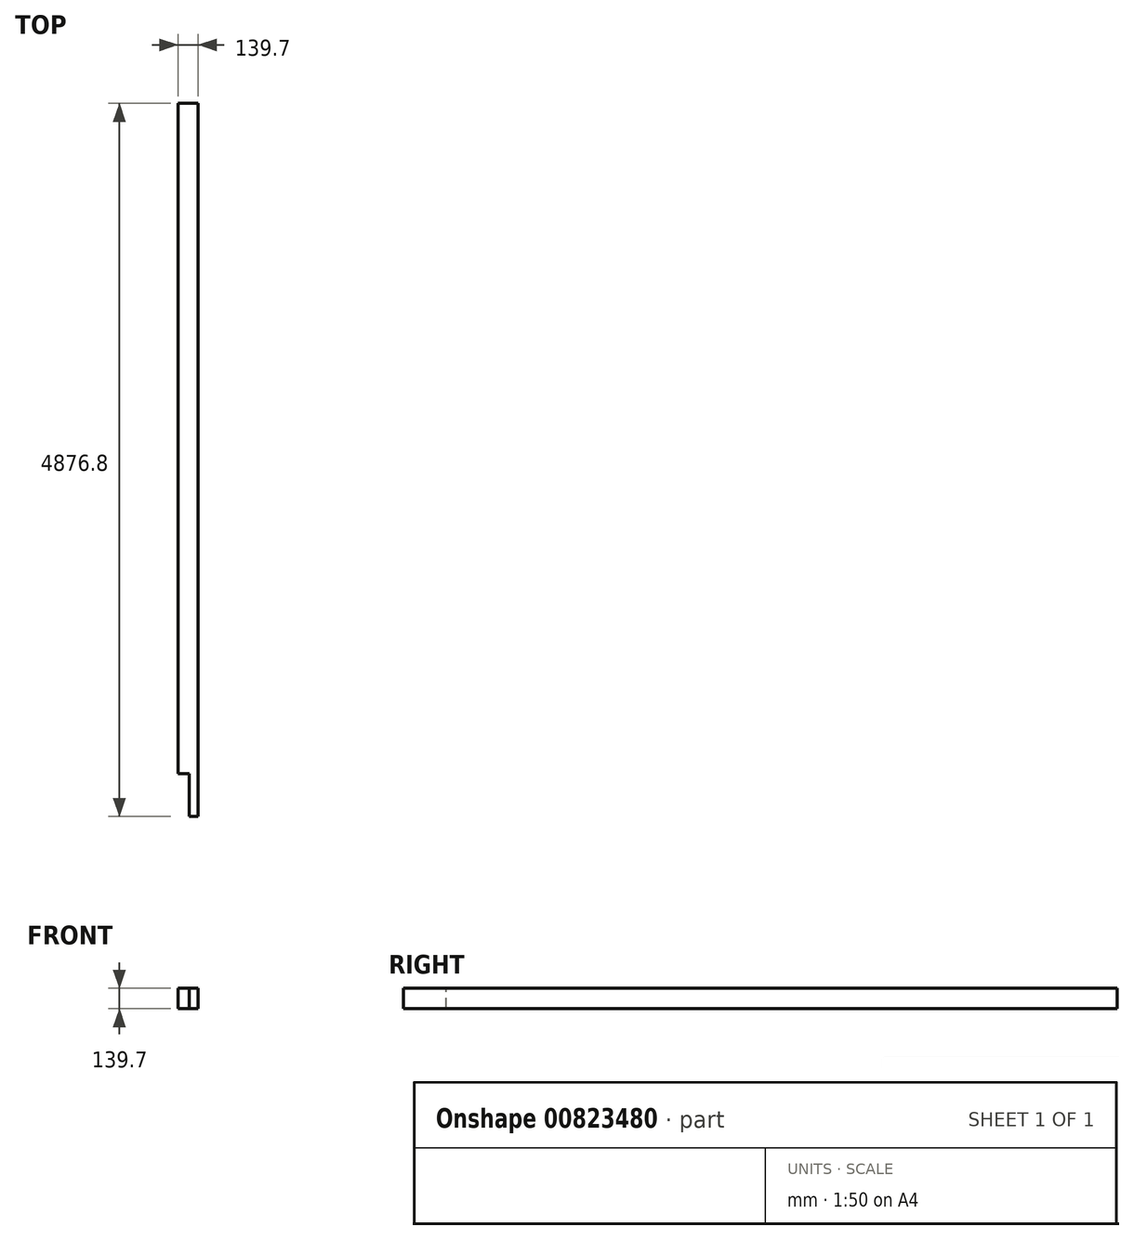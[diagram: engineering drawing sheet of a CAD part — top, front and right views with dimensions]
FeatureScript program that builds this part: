
annotation { "Feature Type Name" : "Feature", "Feature Type Description" : "" }
export const myFeature = defineFeature(function(context is Context, id is Id, definition is map)
    precondition{}
    {
        {
            var Q0;
            Q0=qCreatedBy(makeId("Front.planeOp"),FACE);
            var sketch = newSketch(context, id + "F0", { "sketchPlane" : qUnion([Q0])});
            skLineSegment(sketch, "E0.bottom", {"start": v(0, 0) * mm, "end": v(139.7, 0) * mm});
            skLineSegment(sketch, "E0.top", {"start": v(0, 139.7) * mm, "end": v(139.7, 139.7) * mm});
            skLineSegment(sketch, "E0.left", {"start": v(0, 0) * mm, "end": v(0, 139.7) * mm});
            skLineSegment(sketch, "E0.right", {"start": v(139.7, 0) * mm, "end": v(139.7, 139.7) * mm});
            skSolve(sketch);
        }
        {
            var Q0;
            Q0 = qSketchRegion(id + "F0", true);
            extrude(context, id + "F1", {"entities" : qUnion([Q0]), "depth" : 4876.8 * mm, "offsetDistance" : 25.4 * mm});
        }
        {
            var Q0;
            Q0=makeQuery(id+"F1.opExtrude","SWEPT_FACE",FACE,{"disambiguationData":[OSD([sQuery(id+"F0.wireOp",EDGE,"E0.top")])]});
            var sketch = newSketch(context, id + "F2", { "sketchPlane" : qUnion([Q0])});
            skLineSegment(sketch, "E1.bottom", {"start": v(0, -4876.8) * mm, "end": v(76.2, -4876.8) * mm});
            skLineSegment(sketch, "E1.top", {"start": v(0, -4584.7) * mm, "end": v(76.2, -4584.7) * mm});
            skLineSegment(sketch, "E1.left", {"start": v(0, -4876.8) * mm, "end": v(0, -4584.7) * mm});
            skLineSegment(sketch, "E1.right", {"start": v(76.2, -4876.8) * mm, "end": v(76.2, -4584.7) * mm});
            skSolve(sketch);
        }
        {
            var Q0;
            Q0 = qSketchRegion(id + "F2", true);
            extrude(context, id + "F3", {"entities" : qUnion([Q0]), "operationType" : NewBodyOperationType.REMOVE, "endBound" : BoundingType.THROUGH_ALL, "oppositeDirection" : true, "depth" : 25.4 * mm, "offsetDistance" : 25.4 * mm});
        }
    });
